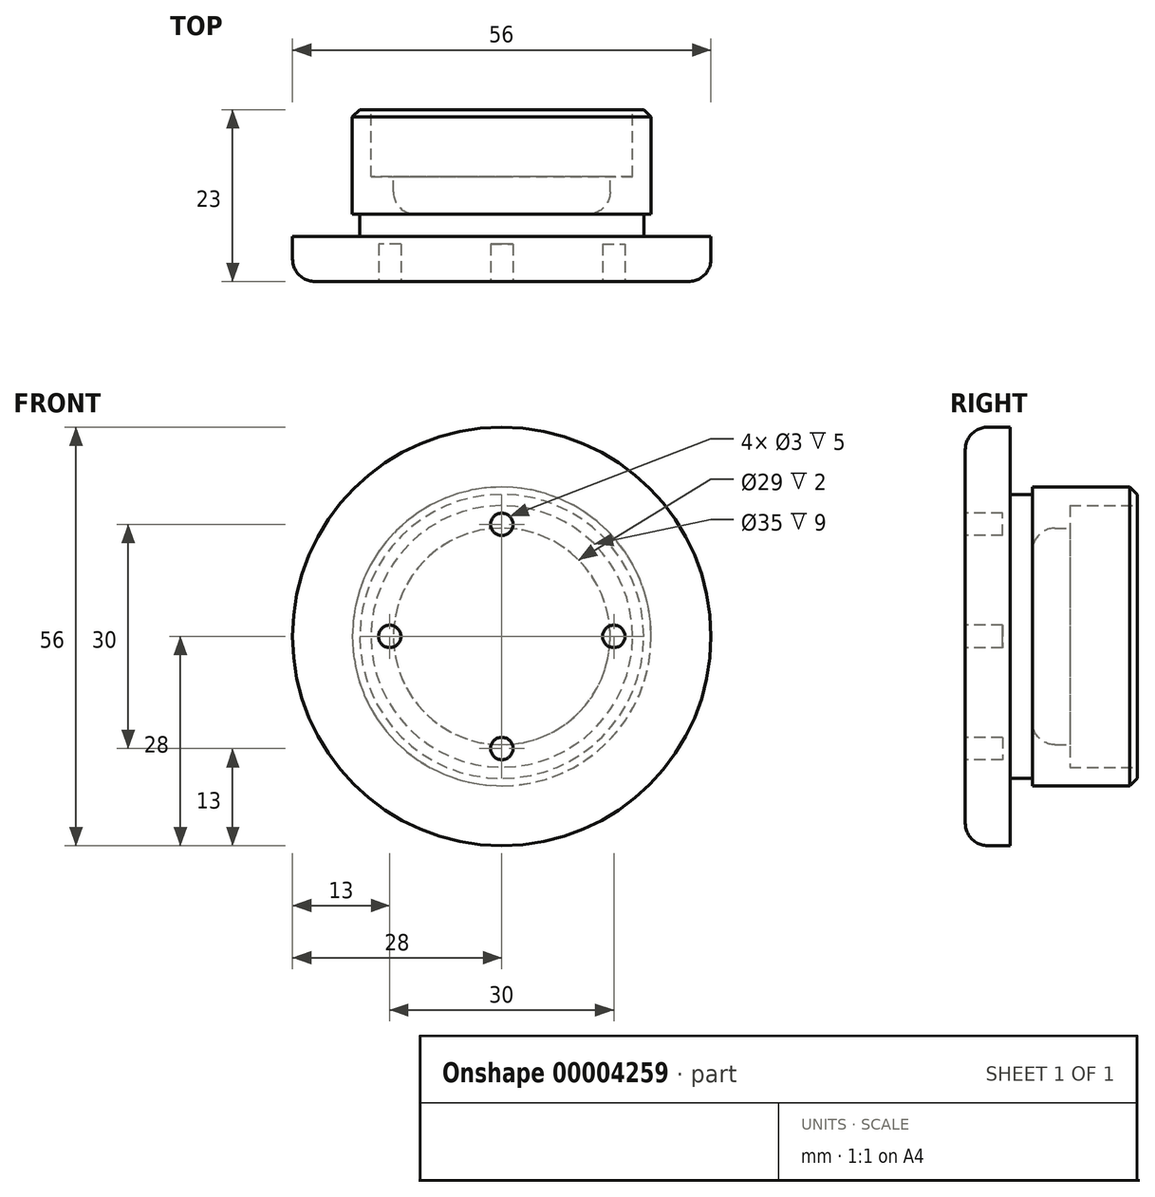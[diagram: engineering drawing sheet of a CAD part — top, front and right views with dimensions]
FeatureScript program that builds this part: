
annotation { "Feature Type Name" : "Feature", "Feature Type Description" : "" }
export const myFeature = defineFeature(function(context is Context, id is Id, definition is map)
    precondition{}
    {
        {
            var Q0;
            Q0=qCreatedBy(makeId("Right.planeOp"),FACE);
            var sketch = newSketch(context, id + "F0", { "sketchPlane" : qUnion([Q0])});
            skLineSegment(sketch, "E0", {"start": v(0, 0) * mm, "end": v(-45.18, 0) * mm, "construction": true});
            skLineSegment(sketch, "E1", {"start": v(-23, 0) * mm, "end": v(-23, 28) * mm});
            skLineSegment(sketch, "E2", {"start": v(-23, 28) * mm, "end": v(-17, 28) * mm});
            skLineSegment(sketch, "E3", {"start": v(-17, 28) * mm, "end": v(-17, 19) * mm});
            skLineSegment(sketch, "E4", {"start": v(-14, 20) * mm, "end": v(-14, 19) * mm});
            skLineSegment(sketch, "E5", {"start": v(-14, 20) * mm, "end": v(0, 20) * mm});
            skLineSegment(sketch, "E6", {"start": v(0, 20) * mm, "end": v(0, 17.5) * mm});
            skLineSegment(sketch, "E7", {"start": v(0, 17.5) * mm, "end": v(-9, 17.5) * mm});
            skLineSegment(sketch, "E8", {"start": v(-9, 17.5) * mm, "end": v(-9, 14.5) * mm});
            skLineSegment(sketch, "E9", {"start": v(-9, 14.5) * mm, "end": v(-14, 14.5) * mm});
            skLineSegment(sketch, "E10", {"start": v(-14, 14.5) * mm, "end": v(-14, 0) * mm});
            skLineSegment(sketch, "E11", {"start": v(-14, 0) * mm, "end": v(-23, 0) * mm});
            skLineSegment(sketch, "E12", {"start": v(-17, 19) * mm, "end": v(-14, 19) * mm});
            skSolve(sketch);
        }
        {
            var Q0;
            Q0=makeQuery(id+"F0.imprint","IMPRINT",FACE,{"disambiguationData":[TD([[makeQuery(id+"F0.imprint","IMPRINT",EDGE,{"derivedFrom":sQuery(id+"F0.wireOp",EDGE,"E1")}),-1.0]])]});
            var Q1;
            Q1=sQuery(id+"F0.wireOp",EDGE,"E0");
            revolve(context, id + "F1", {"entities" : qUnion([Q0]), "axis" : qUnion([Q1]), "revolveType" : RevolveType.FULL});
        }
        {
            var Q0;
            Q0=makeQuery(id+"F1.opRevolve","SWEPT_FACE",FACE,{"disambiguationData":[OSD([sQuery(id+"F0.wireOp",EDGE,"E1")])]});
            var sketch = newSketch(context, id + "F2", { "sketchPlane" : qUnion([Q0])});
            skCircle(sketch, "E13", {"center": v(0, 15) * mm, "radius": 1.5 * mm});
            skCircle(sketch, "E14", {"center": v(0, 0) * mm, "radius": 15 * mm, "construction": true});
            skSolve(sketch);
        }
        {
            var Q0;
            Q0 = qSketchRegion(id + "F2", true);
            extrude(context, id + "F3", {"entities" : qUnion([Q0]), "operationType" : NewBodyOperationType.REMOVE, "oppositeDirection" : true, "depth" : 5 * mm});
        }
        {
            var Q0;
            Q0=makeQuery(id+"F3.boolean.opBoolean","COPY",FACE,{"derivedFrom":makeQuery(id+"F3.opExtrude","SWEPT_FACE",FACE,{"disambiguationData":[OSD([sQuery(id+"F2.wireOp",EDGE,"E13")])]})});
            var Q1;
            Q1=makeQuery(id+"F3.boolean.opBoolean","COPY",FACE,{"derivedFrom":makeQuery(id+"F3.opExtrude","CAP_FACE",FACE,{"disambiguationData":[OSD([sQuery(id+"F2.wireOp",EDGE,"E13")])],"isStart":false})});
            var Q2;
            Q2=makeQuery(id+"F1.opRevolve","SWEPT_FACE",FACE,{"disambiguationData":[OSD([sQuery(id+"F0.wireOp",EDGE,"E2")])]});
            circularPattern(context, id + "F4", {"faces" : qUnion([Q0, Q1]), "axis" : qUnion([Q2]), "angle" : 360 * degree, "instanceCount" : 4, "equalSpace" : true, "patternType" : PatternType.FACE});
        }
        {
            var Q0;
            Q0=makeQuery(id+"F1.opRevolve","SWEPT_EDGE",EDGE,{"disambiguationData":[OSD([sQuery(id+"F0.wireOp",EDGE,"E1"),sQuery(id+"F0.wireOp",EDGE,"E2")])]});
            var Q1;
            Q1=makeQuery(id+"F1.opRevolve","SWEPT_EDGE",EDGE,{"disambiguationData":[OSD([sQuery(id+"F0.wireOp",EDGE,"E9"),sQuery(id+"F0.wireOp",EDGE,"E10")])]});
            fillet(context, id + "F5", {"entities" : qUnion([Q0, Q1]), "radius" : 3 * mm, "tangentPropagation" : true, "allowEdgeOverflow" : false});
        }
        {
            var Q0;
            Q0=makeQuery(id+"F1.opRevolve","SWEPT_EDGE",EDGE,{"disambiguationData":[OSD([sQuery(id+"F0.wireOp",EDGE,"E5"),sQuery(id+"F0.wireOp",EDGE,"E6")])]});
            chamfer(context, id + "F6", {"entities" : qUnion([Q0]), "width" : 1 * mm, "tangentPropagation" : true});
        }
    });
